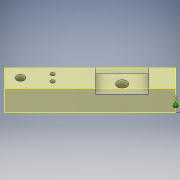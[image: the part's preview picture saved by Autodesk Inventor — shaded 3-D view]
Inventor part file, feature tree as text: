
AUTODESK INVENTOR PART (.ipt)
format: ipt  version: 2018 (Build 220112000, 112)  size: 480,768 bytes
history: native  units: in
note: dims shown in document units (in); Inventor stores cm internally (conversion verified against a paired STEP export)
features: sketch x8, extrude x7, other x1, hole x1, thread x1
ambient origin geometry x8: Origin, YZ Plane, XZ Plane, XY Plane, X Axis, Y Axis, Z Axis, Center Point
bodies: Solid1 (feature_tree)
feature tree (18):
  other  "Standard"
  extrude  "Extrusion1"  Depth=4.0in
  extrude  "Extrusion3"  Depth=1.25in
  extrude  "Extrusion4"  Depth=0.74in
  extrude  "Extrusion5"  Depth=0.187in
  extrude  "Extrusion6"  Depth=0.37in
  extrude  "Extrusion7"  Depth=0.25in
  extrude  "Extrusion8"  Depth=0.37in
  hole  "Hole1"  [1 undecoded]
  thread  "Thread1"  [1 undecoded]
  sketch  "Sketch1"  dims[d0=0.74in d1=4.0in]
  sketch  "Sketch2"  dims[d2=0.74in d3=0.0in d4=1.25in]
  sketch  "Sketch3"  dims[d5=0.625in d6=0.74in]
  sketch  "Sketch4"  dims[d9=0.187in d10=0.0in d11=0.312in]
  sketch  "Sketch5"  dims[d12=0.625in d13=0.37in]
  sketch  "Sketch6"  dims[d14=0.6in d15=0.0in d16=0.25in]
  sketch  "Sketch7"  dims[d17=0.375in d18=0.37in]
  sketch  "Sketch9"  dims[d19=0.8in d20=0.0in d21=0.125in d22=0.125in d23=1.125in d24=1.125in d25=0.0687in d26=0.0687in d27=0.8in d28=0.0in d29=0.125in d31=0.0687in d32=1.125in d33=0.437in d34=0.0in d35=0.125in d36=0.365in d37=1.125in d38=0.3in d39=0.0in d43=0.25in d44=0.75in d45=0.375in d46=0.25in d47=0.5635in d48=0.75in d49=0.8108in d50=1.0in d51=0.0in]
note: 2 required parameter values undecoded (feature->parameter linkage not recoverable at this tier; creation-order binding heuristic only, values carry confidence <= 0.55)
